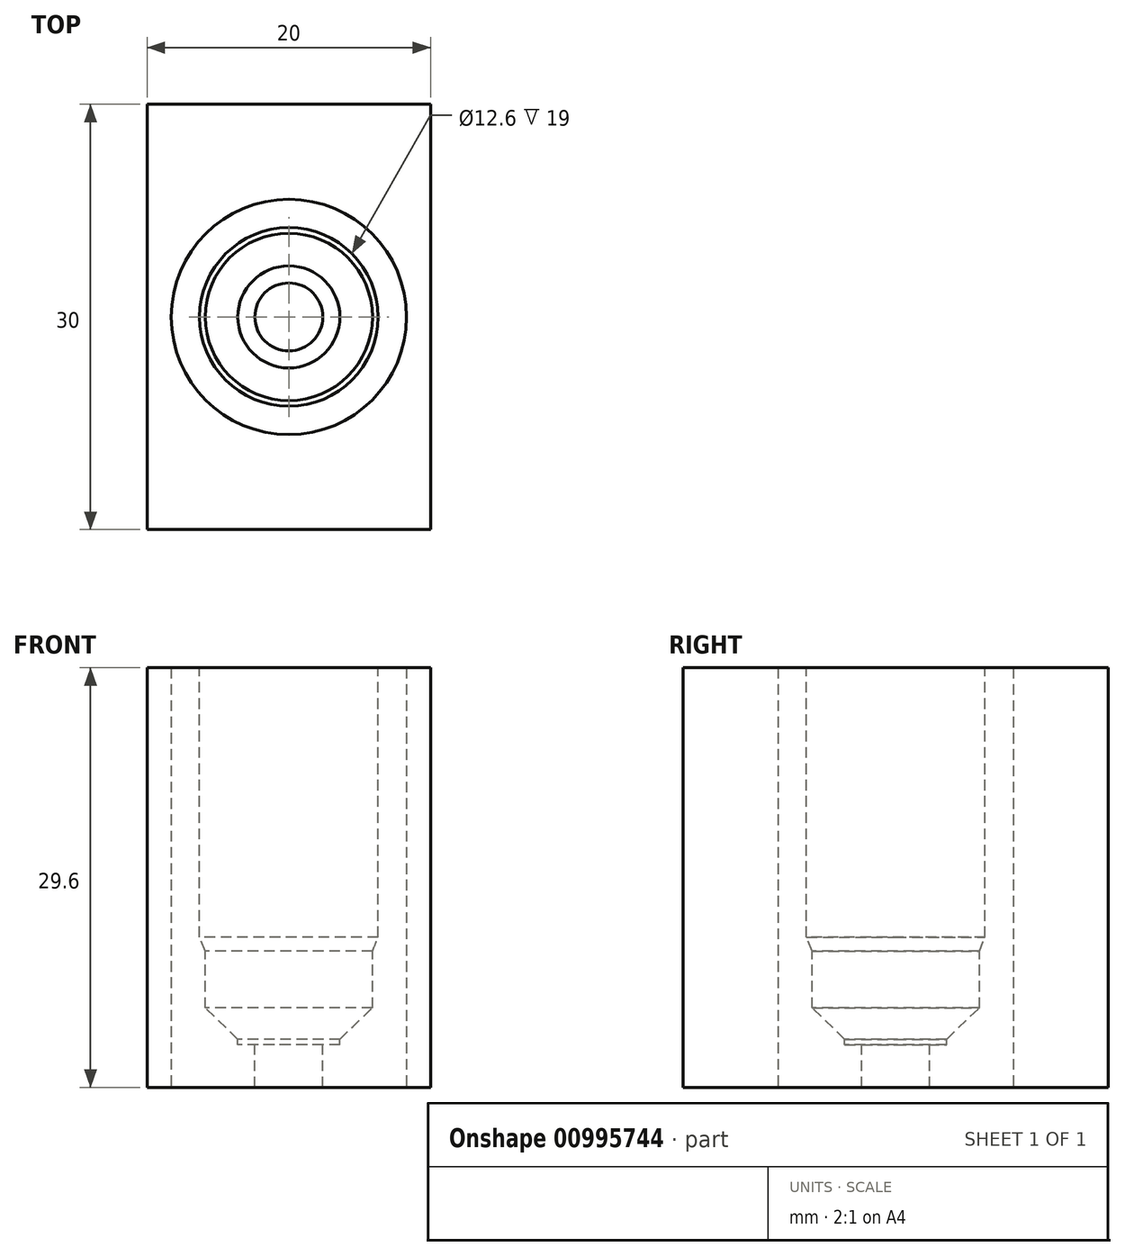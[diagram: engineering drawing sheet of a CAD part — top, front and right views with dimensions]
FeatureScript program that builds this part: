
annotation { "Feature Type Name" : "Feature", "Feature Type Description" : "" }
export const myFeature = defineFeature(function(context is Context, id is Id, definition is map)
    precondition{}
    {
        {
            var Q0;
            Q0=qCreatedBy(makeId("Front.planeOp"),FACE);
            var sketch = newSketch(context, id + "F0", { "sketchPlane" : qUnion([Q0])});
            skLineSegment(sketch, "E0", {"start": v(-3.6, 3.4) * mm, "end": v(-5.9, 5.6) * mm});
            skLineSegment(sketch, "E1", {"start": v(-5.9, 5.6) * mm, "end": v(-5.9, 9.6) * mm});
            skLineSegment(sketch, "E2", {"start": v(-5.9, 9.6) * mm, "end": v(-6.3, 10.6) * mm});
            skLineSegment(sketch, "E3", {"start": v(-6.3, 10.6) * mm, "end": v(-6.3, 29.6) * mm});
            skLineSegment(sketch, "E4", {"start": v(-6.3, 29.6) * mm, "end": v(0, 29.6) * mm});
            skLineSegment(sketch, "E5", {"start": v(0, 29.6) * mm, "end": v(0, 0) * mm});
            skLineSegment(sketch, "E6.top", {"start": v(-2.4, 0) * mm, "end": v(0, 0) * mm});
            skLineSegment(sketch, "E6.right", {"start": v(0, 0) * mm, "end": v(0, 0) * mm});
            skLineSegment(sketch, "E7", {"start": v(-6.3, 29.6) * mm, "end": v(-8.3, 29.6) * mm});
            skLineSegment(sketch, "E8", {"start": v(-8.3, 29.6) * mm, "end": v(-8.3, 0) * mm});
            skLineSegment(sketch, "E9", {"start": v(-2.4, 3) * mm, "end": v(-2.4, 0) * mm});
            skLineSegment(sketch, "E10", {"start": v(-2.4, 3) * mm, "end": v(-3.6, 3) * mm});
            skLineSegment(sketch, "E11", {"start": v(-3.6, 3) * mm, "end": v(-3.6, 3.4) * mm});
            skLineSegment(sketch, "E12", {"start": v(-8.3, 0) * mm, "end": v(-2.4, 0) * mm});
            skSolve(sketch);
        }
        {
            var Q0;
            Q0=makeQuery(id+"F0.imprint","IMPRINT",FACE,{"disambiguationData":[TD([[makeQuery(id+"F0.imprint","IMPRINT",EDGE,{"derivedFrom":sQuery(id+"F0.wireOp",EDGE,"E0")}),1.0]])]});
            var Q1;
            Q1=sQuery(id+"F0.wireOp",EDGE,"E7");
            var Q2;
            Q2=sQuery(id+"F0.wireOp",EDGE,"E3");
            var Q3;
            Q3=sQuery(id+"F0.wireOp",EDGE,"E2");
            var Q4;
            Q4=sQuery(id+"F0.wireOp",EDGE,"E1");
            var Q5;
            Q5=sQuery(id+"F0.wireOp",EDGE,"E0");
            var Q6;
            Q6=sQuery(id+"F0.wireOp",EDGE,"E11");
            var Q7;
            Q7=sQuery(id+"F0.wireOp",EDGE,"E10");
            var Q8;
            Q8=sQuery(id+"F0.wireOp",EDGE,"E9");
            var Q9;
            Q9=sQuery(id+"F0.wireOp",EDGE,"E12");
            var Q10;
            Q10=sQuery(id+"F0.wireOp",EDGE,"E8");
            var Q11;
            Q11=sQuery(id+"F0.wireOp",EDGE,"E5");
            revolve(context, id + "F1", {"surfaceOperationType" : NewSurfaceOperationType.NEW, "entities" : qUnion([Q0]), "surfaceEntities" : qUnion([Q1, Q2, Q3, Q4, Q5, Q6, Q7, Q8, Q9, Q10]), "axis" : qUnion([Q11]), "revolveType" : RevolveType.FULL});
        }
        {
            var Q0;
            Q0=makeQuery(id+"F1.opRevolve","SWEPT_FACE",FACE,{"disambiguationData":[OSD([sQuery(id+"F0.wireOp",EDGE,"E12")])]});
            var sketch = newSketch(context, id + "F2", { "sketchPlane" : qUnion([Q0])});
            skLineSegment(sketch, "E13.bottom", {"start": v(10, -15) * mm, "end": v(-10, -15) * mm});
            skLineSegment(sketch, "E13.top", {"start": v(10, 15) * mm, "end": v(-10, 15) * mm});
            skLineSegment(sketch, "E13.left", {"start": v(10, -15) * mm, "end": v(10, 15) * mm});
            skLineSegment(sketch, "E13.right", {"start": v(-10, -15) * mm, "end": v(-10, 15) * mm});
            skPoint(sketch, "E13.middle", {"position": v(0, 0) * mm});
            skSolve(sketch);
        }
        {
            var Q0;
            Q0=makeQuery(id+"F2.imprint","IMPRINT",FACE,{"disambiguationData":[TD([[makeQuery(id+"F2.imprint","IMPRINT",EDGE,{"derivedFrom":sQuery(id+"F2.wireOp",EDGE,"E13.bottom")}),-1.0]])]});
            var Q1;
            {var subQ0=sQuery(id+"F2.wireOp",EDGE,"E13.right");var subQ1=sQuery(id+"F2.wireOp",EDGE,"E13.top");var subQ2=makeQuery(id+"F2.imprint","INTERSECT",VERTEX,{"derivedFrom":[subQ1,subQ0]});Q1=makeQuery(id+"F2.imprint","IMPRINT",FACE,{"disambiguationData":[TD([[makeQuery(id+"F2.imprint","IMPRINT",EDGE,{"disambiguationData":[TD([[subQ2,1.0]])],"derivedFrom":subQ1}),1.0]])]});}
            var Q2;
            {var subQ0=sQuery(id+"F2.wireOp",EDGE,"E13.left");var subQ1=sQuery(id+"F2.wireOp",EDGE,"E13.top");var subQ2=makeQuery(id+"F2.imprint","INTERSECT",VERTEX,{"derivedFrom":[subQ1,subQ0]});Q2=makeQuery(id+"F2.imprint","IMPRINT",FACE,{"disambiguationData":[TD([[makeQuery(id+"F2.imprint","IMPRINT",EDGE,{"disambiguationData":[TD([[subQ2,-1.0]])],"derivedFrom":subQ1}),1.0]])]});}
            extrude(context, id + "F3", {"entities" : qUnion([Q0, Q1, Q2]), "oppositeDirection" : true, "depth" : 29.6 * mm, "offsetDistance" : 25 * mm});
        }
    });
